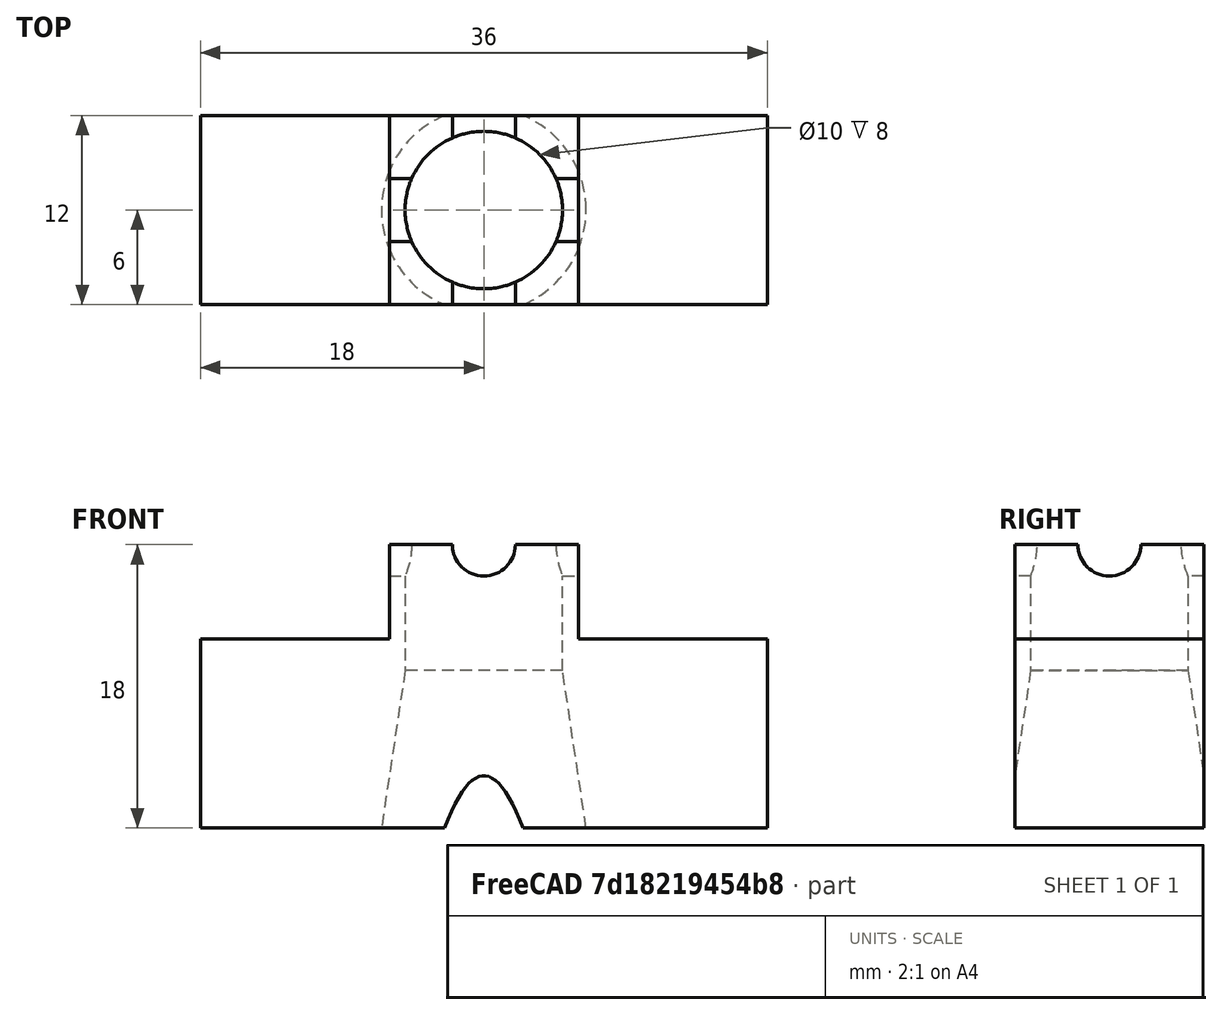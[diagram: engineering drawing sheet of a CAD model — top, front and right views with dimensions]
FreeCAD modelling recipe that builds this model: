
FCSTD DOCUMENT  (FreeCAD 0.18R4 (GitTag))
Label: snubInsert0
License: All rights reserved
LicenseURL: http://en.wikipedia.org/wiki/All_rights_reserved
objects: Part::Cylinder×7, Part::Cut×6, Part::MultiFuse×6, Part::Box×5, Part::Cone×1, Part::Feature×1
note: 26 computed .brp shape members not serialized (recipe doc carries the construction recipe); baked Part::Feature solids carry a one-line shape summary decoded from their .brp

FEATURE [Part::Box] Box  label="Cube"
  AttacherType = Attacher::AttachEngine3D
  Height = 45
  Length = 12
  Width = 12
FEATURE [Part::Cylinder] Cylinder
  Angle = 360
  AttacherType = Attacher::AttachEngine3D
  Height = 54
  Placement = pos=(6,6,-5.75) rot=(0,0,1;0rad)
  Radius = 5
FEATURE [Part::Cylinder] Cylinder001
  Angle = 360
  AttacherType = Attacher::AttachEngine3D
  Height = 4
  Placement = pos=(0,-10.5,0) rot=(0,0,1;0rad)
  Radius = 5
FEATURE [Part::Cylinder] Cylinder002
  Angle = 360
  AttacherType = Attacher::AttachEngine3D
  Height = 4
  Placement = pos=(0,-10.5,0) rot=(0,0,1;0rad)
  Radius = 2
FEATURE [Part::Cut] Cut001
  Base = -> Cylinder001
  Placement = pos=(6,16.5,0) rot=(0,0,1;0rad)
  Tool = -> Cylinder002
FEATURE [Part::Cut] Cut
  Base = -> Box
  Tool = -> Cylinder
FEATURE [Part::MultiFuse] Fusion
  Shapes = -> [Cut001,Cut]
FEATURE [Part::Box] Box001  label="Cube001"
  AttacherType = Attacher::AttachEngine3D
  Height = 12
  Length = 12
  Placement = pos=(-12,0,0) rot=(0,0,1;0rad)
  Width = 12
FEATURE [Part::Box] Box002  label="Cube002"
  AttacherType = Attacher::AttachEngine3D
  Height = 12
  Length = 12
  Placement = pos=(12,0,0) rot=(0,0,1;0rad)
  Width = 12
FEATURE [Part::MultiFuse] Fusion001
  Shapes = -> [Box002,Fusion]
FEATURE [Part::MultiFuse] Fusion002
  Shapes = -> [Fusion001,Box001]
FEATURE [Part::Cone] Cone
  Angle = 360
  AttacherType = Attacher::AttachEngine3D
  Height = 10
  Placement = pos=(6,6,0) rot=(0,0,1;0rad)
  Radius1 = 6.5
  Radius2 = 5
FEATURE [Part::Cut] Cut002
  Base = -> Fusion002
  Tool = -> Cone
FEATURE [Part::Box] Box003  label="Cube003"
  AttacherType = Attacher::AttachEngine3D
  Height = 12
  Length = 36
  Placement = pos=(-12,-2,0) rot=(0,0,1;0rad)
  Width = 2
FEATURE [Part::Cylinder] Cylinder003
  Angle = 360
  AttacherType = Attacher::AttachEngine3D
  Height = 20
  Placement = pos=(-4,6,47) rot=(0,1,0;1.5708rad)
  Radius = 2
FEATURE [Part::Cylinder] Cylinder004
  Angle = 360
  AttacherType = Attacher::AttachEngine3D
  Height = 20
  Placement = pos=(6,15,47) rot=(0.57735,0.57735,-0.57735;2.0944rad)
  Radius = 2
FEATURE [Part::MultiFuse] Fusion003
  Placement = pos=(0,0,-29) rot=(0,0,1;0rad)
  Shapes = -> [Cylinder003,Cylinder004]
FEATURE [Part::Cylinder] Cylinder005
  Angle = 360
  AttacherType = Attacher::AttachEngine3D
  Height = 20
  Placement = pos=(-4,6,47) rot=(0,1,0;1.5708rad)
  Radius = 2
FEATURE [Part::Cylinder] Cylinder006
  Angle = 360
  AttacherType = Attacher::AttachEngine3D
  Height = 20
  Placement = pos=(6,15,47) rot=(0.57735,0.57735,-0.57735;2.0944rad)
  Radius = 2
FEATURE [Part::MultiFuse] Fusion004
  Placement = pos=(-1.67303,1.48356,-9) rot=(0,0,-1;0.261799rad)
  Shapes = -> [Cylinder005,Cylinder006]
FEATURE [Part::MultiFuse] Fusion005
  Shapes = -> [Fusion004,Fusion003]
FEATURE [Part::Cut] Cut003
  Base = -> Cut002
  Tool = -> Fusion005
FEATURE [Part::Cut] Cut004
  Base = -> Cut003
  Tool = -> Box003
FEATURE [Part::Box] Box004  label="Cube004"
  AttacherType = Attacher::AttachEngine3D
  Height = 40
  Length = 20
  Placement = pos=(0,0,18) rot=(0,0,1;0rad)
  Width = 30
FEATURE [Part::Cut] Cut005
  Base = -> Cut004
  Tool = -> Box004
FEATURE [Part::Feature] Cut005_solid  label="Cut005 (Solid)"
  shape: bbox 36 x 13 x 18 mm, 33 faces (baked)
